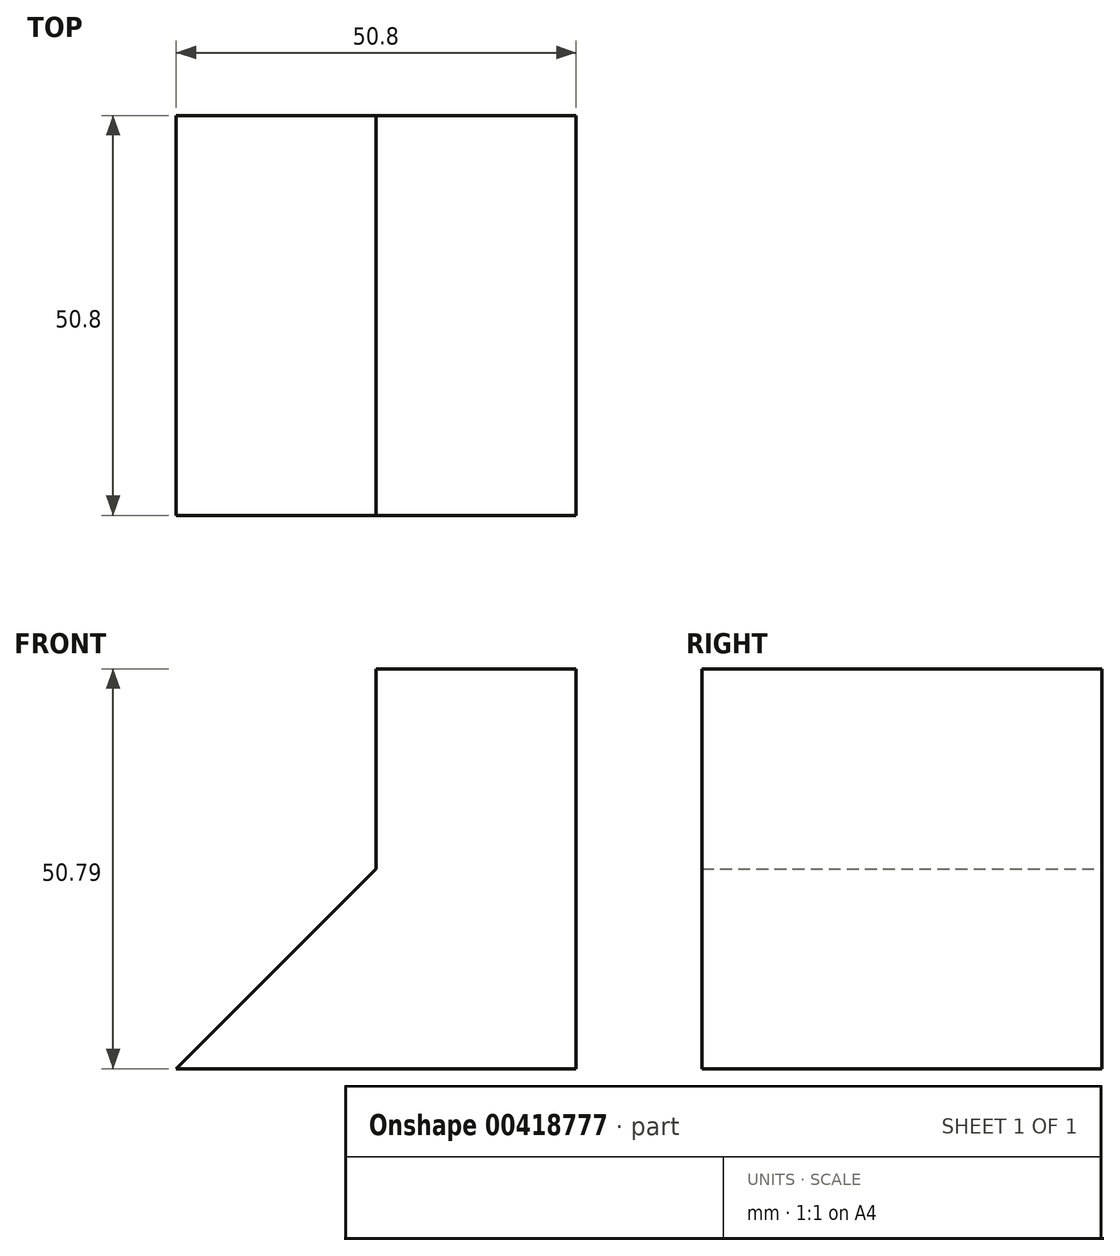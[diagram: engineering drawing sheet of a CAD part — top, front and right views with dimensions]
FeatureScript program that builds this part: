
annotation { "Feature Type Name" : "Feature", "Feature Type Description" : "" }
export const myFeature = defineFeature(function(context is Context, id is Id, definition is map)
    precondition{}
    {
        {
            var Q0;
            Q0=qCreatedBy(makeId("Front.planeOp"),FACE);
            var sketch = newSketch(context, id + "F0", { "sketchPlane" : qUnion([Q0])});
            skLineSegment(sketch, "E0", {"start": v(0, 0) * mm, "end": v(-50.8, 0) * mm});
            skLineSegment(sketch, "E1", {"start": v(-50.8, 0) * mm, "end": v(-25.4, 25.4) * mm});
            skLineSegment(sketch, "E2", {"start": v(-25.4, 25.4) * mm, "end": v(-25.4, 50.8) * mm});
            skLineSegment(sketch, "E3", {"start": v(-25.4, 50.8) * mm, "end": v(0, 50.8) * mm});
            skLineSegment(sketch, "E4", {"start": v(0, 50.8) * mm, "end": v(0, 0) * mm});
            skSolve(sketch);
        }
        {
            var Q0;
            Q0 = qSketchRegion(id + "F0", true);
            extrude(context, id + "F1", {"entities" : qUnion([Q0]), "depth" : 50.8 * mm});
        }
    });
